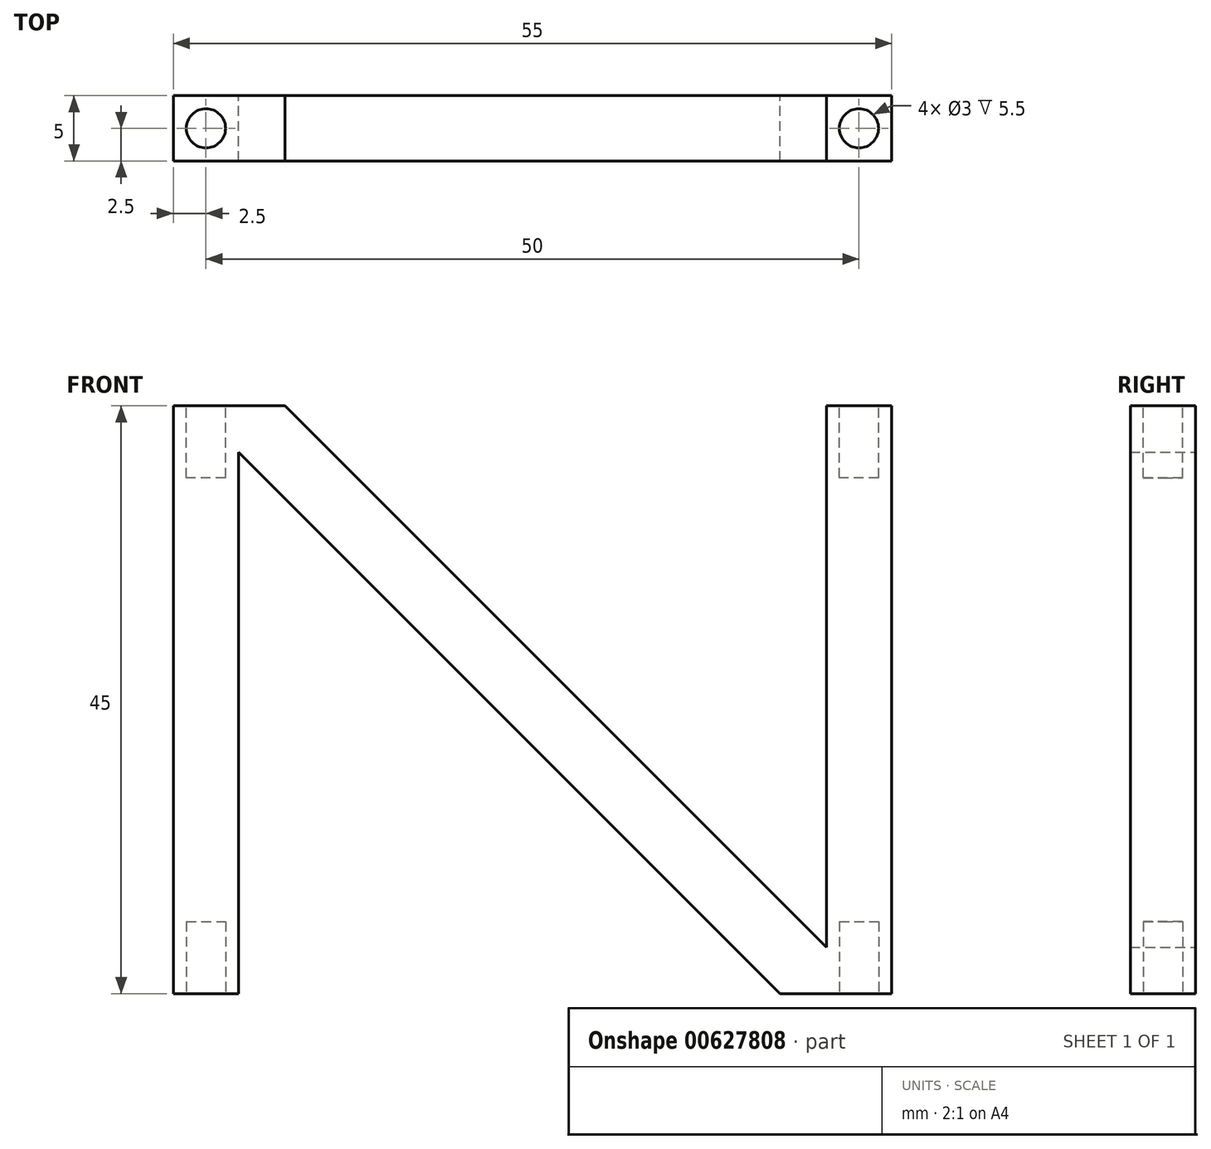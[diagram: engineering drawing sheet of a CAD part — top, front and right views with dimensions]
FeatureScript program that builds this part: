
annotation { "Feature Type Name" : "Feature", "Feature Type Description" : "" }
export const myFeature = defineFeature(function(context is Context, id is Id, definition is map)
    precondition{}
    {
        {
            var Q0;
            Q0=qCreatedBy(makeId("Front.planeOp"),FACE);
            var sketch = newSketch(context, id + "F0", { "sketchPlane" : qUnion([Q0])});
            skLineSegment(sketch, "E0", {"start": v(-55, 45) * mm, "end": v(-55, 0) * mm});
            skLineSegment(sketch, "E1", {"start": v(-50, 41.46) * mm, "end": v(-50, 0) * mm});
            skLineSegment(sketch, "E2", {"start": v(-5, 3.54) * mm, "end": v(-5, 45) * mm});
            skLineSegment(sketch, "E3", {"start": v(0, 45) * mm, "end": v(0, 0) * mm});
            skLineSegment(sketch, "E4", {"start": v(-46.46, 45) * mm, "end": v(-5, 3.54) * mm});
            skLineSegment(sketch, "E5", {"start": v(-8.54, 0) * mm, "end": v(-50, 41.46) * mm});
            skLineSegment(sketch, "E6", {"start": v(-46.46, 45) * mm, "end": v(-55, 45) * mm});
            skLineSegment(sketch, "E7", {"start": v(-50, 0) * mm, "end": v(-55, 0) * mm});
            skLineSegment(sketch, "E8", {"start": v(-5, 45) * mm, "end": v(0, 45) * mm});
            skLineSegment(sketch, "E9", {"start": v(-8.54, 0) * mm, "end": v(0, 0) * mm});
            skPoint(sketch, "E10.end.orphan", {"position": v(0, 0) * mm});
            skPoint(sketch, "E11.orphan", {"position": v(-55, 0) * mm});
            skLineSegment(sketch, "E12", {"start": v(-50, 0) * mm, "end": v(-8.54, 0) * mm, "construction": true});
            skSolve(sketch);
        }
        {
            var Q0;
            Q0=makeQuery(id+"F0.imprint","IMPRINT",FACE,{"disambiguationData":[TD([[makeQuery(id+"F0.imprint","IMPRINT",EDGE,{"derivedFrom":sQuery(id+"F0.wireOp",EDGE,"E0")}),1.0]])]});
            extrude(context, id + "F1", {"entities" : qUnion([Q0]), "depth" : 5 * mm, "offsetDistance" : 25 * mm});
        }
        {
            var Q0;
            Q0=makeQuery(id+"F1.opExtrude","SWEPT_FACE",FACE,{"disambiguationData":[OSD([sQuery(id+"F0.wireOp",EDGE,"E6")])]});
            var sketch = newSketch(context, id + "F2", { "sketchPlane" : qUnion([Q0])});
            skCircle(sketch, "E13", {"center": v(-52.5, -2.5) * mm, "radius": 1.5 * mm});
            skCircle(sketch, "E14", {"center": v(-2.5, -2.5) * mm, "radius": 1.5 * mm});
            skCircle(sketch, "E15", {"center": v(101.68, -24.66) * mm, "radius": 4.12 * mm});
            skSolve(sketch);
        }
        {
            var Q0;
            Q0 = qSketchRegion(id + "F2", true);
            extrude(context, id + "F3", {"entities" : qUnion([Q0]), "operationType" : NewBodyOperationType.REMOVE, "oppositeDirection" : true, "depth" : 5.5 * mm, "offsetDistance" : 25 * mm});
        }
        {
            var Q0;
            Q0=makeQuery(id+"F1.opExtrude","SWEPT_FACE",FACE,{"disambiguationData":[OSD([sQuery(id+"F0.wireOp",EDGE,"E7")])]});
            var sketch = newSketch(context, id + "F4", { "sketchPlane" : qUnion([Q0])});
            skCircle(sketch, "E16", {"center": v(-52.5, 2.5) * mm, "radius": 1.5 * mm});
            skPoint(sketch, "E16.centerSnap0", {"position": v(-55, 2.5) * mm});
            skCircle(sketch, "E17", {"center": v(-2.5, 2.5) * mm, "radius": 1.5 * mm});
            skSolve(sketch);
        }
        {
            var Q0;
            Q0 = qSketchRegion(id + "F4", true);
            extrude(context, id + "F5", {"entities" : qUnion([Q0]), "operationType" : NewBodyOperationType.REMOVE, "oppositeDirection" : true, "depth" : 5.5 * mm, "offsetDistance" : 25 * mm});
        }
    });
